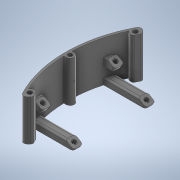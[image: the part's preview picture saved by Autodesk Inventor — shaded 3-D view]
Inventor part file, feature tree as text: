
AUTODESK INVENTOR PART (.ipt)
format: ipt  version: 2020 (Build 240168000, 168)  size: 1,409,024 bytes
history: native  units: mm
features: projected_geometry x32, extrude x20, sketch x13, other x9, fillet x1
ambient origin geometry x8: Origin, YZ Plane, XZ Plane, XY Plane, X Axis, Y Axis, Z Axis, Center Point
bodies: Body1 (feature_tree)
feature tree (75):
  other  "Твердое тело1"
  extrude  "outer"  TaperAngle=45.0deg  [1 undecoded]
  extrude  "inner"  Depth=7.0mm
  sketch  "Эскиз3"
  extrude  "Выдавливание3"  Depth=20.0mm
  extrude  "Выдавливание4"  Depth=7.0mm
  sketch  "Эскиз4"
  extrude  "Выдавливание5"  Depth=3.2mm
  extrude  "Выдавливание6"  Depth=59.0mm
  sketch  "Эскиз5"
  extrude  "Выдавливание7"  Depth=83.0mm
  extrude  "Выдавливание8"  Depth=69.0mm
  sketch  "Эскиз6"
  extrude  "Выдавливание9"  Depth=55.0mm
  extrude  "Выдавливание10"  Depth=3.0mm
  fillet  "Сопряжение1"  Radius=8.0mm
  other  "РабПлоскость2"
  other  "РабПлоскость3"
  sketch  "Эскиз10"
  sketch  "Эскиз11"
  other  "РабПлоскость4"
  other  "РабПлоскость5"
  other  "РабОсь2"
  other  "РабОсь1"
  sketch  "Эскиз12"
  extrude  "Выдавливание12"  Depth=5.0mm
  sketch  "Эскиз8"
  extrude  "asterisk"  Depth=2.0mm
  other  "РабПлоскость7"
  sketch  "Эскиз13"
  extrude  "Выдавливание13"  Depth=40.0mm TaperAngle=360.0deg
  extrude  "Выдавливание14"  Depth=2.0mm
  extrude  "Выдавливание15"  Depth=105.0mm
  extrude  "Выдавливание17"  Depth=2.0mm
  extrude  "Выдавливание18"  Depth=2.0mm TaperAngle=0.0deg
  extrude  "Выдавливание16"  Depth=3.5mm
  extrude  "Выдавливание19"  Depth=2.0mm
  extrude  "Выдавливание20"  Depth=6.0mm
  sketch  "Эскиз1"
  sketch  "Эскиз2"
  projected_geometry  "Спроецированная петля1"
  projected_geometry  "Спроецированная петля2"
  projected_geometry  "Спроецированная петля3"
  projected_geometry  "Спроецированная петля4"
  projected_geometry  "Спроецированная петля5"
  projected_geometry  "Спроецированная петля8"
  projected_geometry  "Спроецированная петля9"
  projected_geometry  "Спроецированная петля10"
  projected_geometry  "Спроецированная петля11"
  projected_geometry  "Спроецированная петля12"
  other  "РабПлоскость6"
  projected_geometry  "Спроецированная петля13"
  projected_geometry  "Спроецированная петля14"
  projected_geometry  "Спроецированная петля15"
  projected_geometry  "Спроецированная петля16"
  projected_geometry  "Спроецированная петля17"
  projected_geometry  "Спроецированная петля18"
  projected_geometry  "Спроецированная петля19"
  projected_geometry  "Спроецированная петля20"
  projected_geometry  "Спроецированная петля21"
  projected_geometry  "Спроецированная петля22"
  projected_geometry  "Спроецированная петля23"
  projected_geometry  "Спроецированная петля24"
  projected_geometry  "Спроецированная петля25"
  projected_geometry  "Спроецированная петля26"
  projected_geometry  "Спроецированная петля27"
  projected_geometry  "Спроецированная петля28"
  projected_geometry  "Спроецированная петля29"
  projected_geometry  "Спроецированная петля30"
  projected_geometry  "Спроецированная петля31"
  projected_geometry  "Спроецированная петля32"
  sketch  "Эскиз14"
  projected_geometry  "Спроецированная петля33"
  sketch  "Эскиз15"
  projected_geometry  "Спроецированная петля34"
note: 1 required parameter value undecoded (feature->parameter linkage not recoverable at this tier; creation-order binding heuristic only, values carry confidence <= 0.55)
